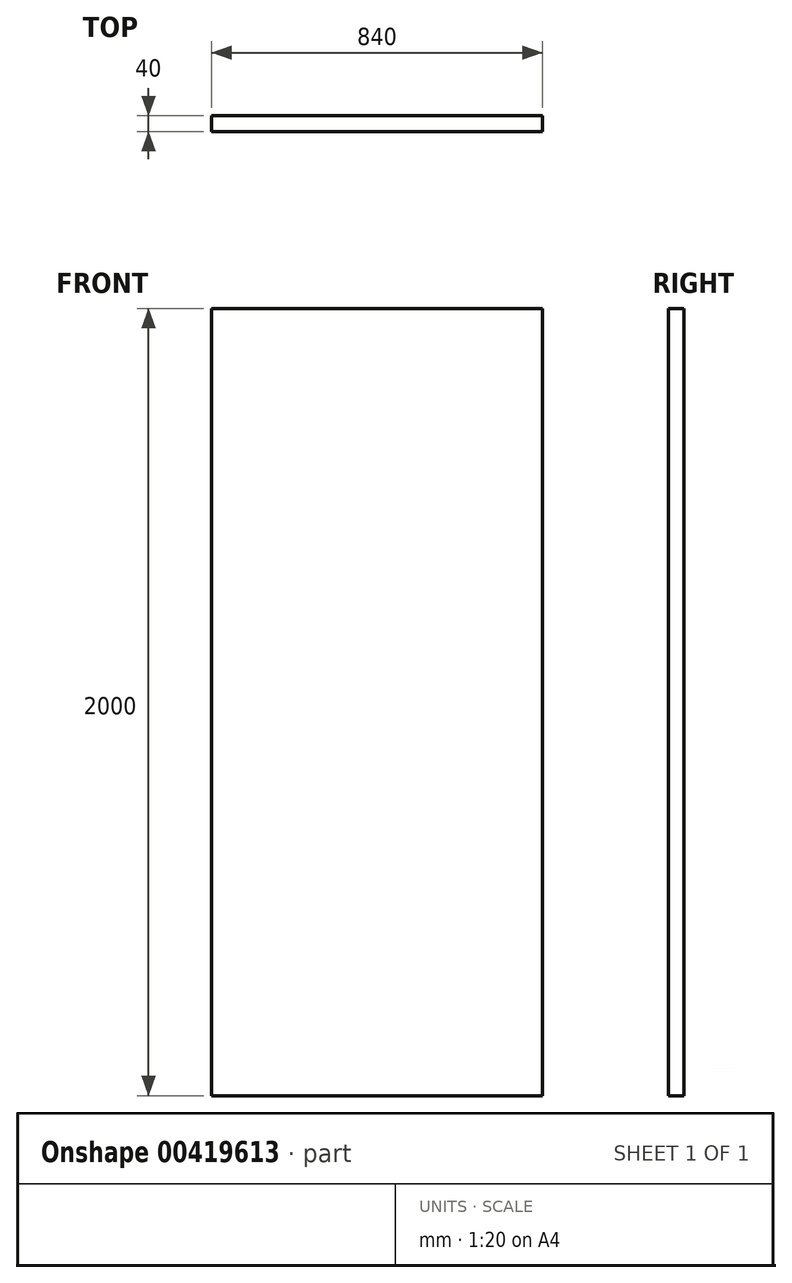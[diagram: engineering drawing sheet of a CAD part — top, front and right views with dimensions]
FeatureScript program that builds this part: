
annotation { "Feature Type Name" : "Feature", "Feature Type Description" : "" }
export const myFeature = defineFeature(function(context is Context, id is Id, definition is map)
    precondition{}
    {
        {
            var Q0;
            Q0=qCreatedBy(makeId("Top.planeOp"),FACE);
            var sketch = newSketch(context, id + "F0", { "sketchPlane" : qUnion([Q0])});
            skLineSegment(sketch, "E0.bottom", {"start": v(-57.52, -43.77) * mm, "end": v(782.48, -43.77) * mm});
            skLineSegment(sketch, "E0.top", {"start": v(-57.52, -3.77) * mm, "end": v(782.48, -3.77) * mm});
            skLineSegment(sketch, "E0.left", {"start": v(-57.52, -43.77) * mm, "end": v(-57.52, -3.77) * mm});
            skLineSegment(sketch, "E0.right", {"start": v(782.48, -43.77) * mm, "end": v(782.48, -3.77) * mm});
            skSolve(sketch);
        }
        {
            var Q0;
            Q0=makeQuery(id+"F0.imprint","IMPRINT",FACE,{"disambiguationData":[TD([[makeQuery(id+"F0.imprint","IMPRINT",EDGE,{"derivedFrom":sQuery(id+"F0.wireOp",EDGE,"E0.bottom")}),1.0]])]});
            extrude(context, id + "F1", {"entities" : qUnion([Q0]), "depth" : 2000 * mm});
        }
    });
